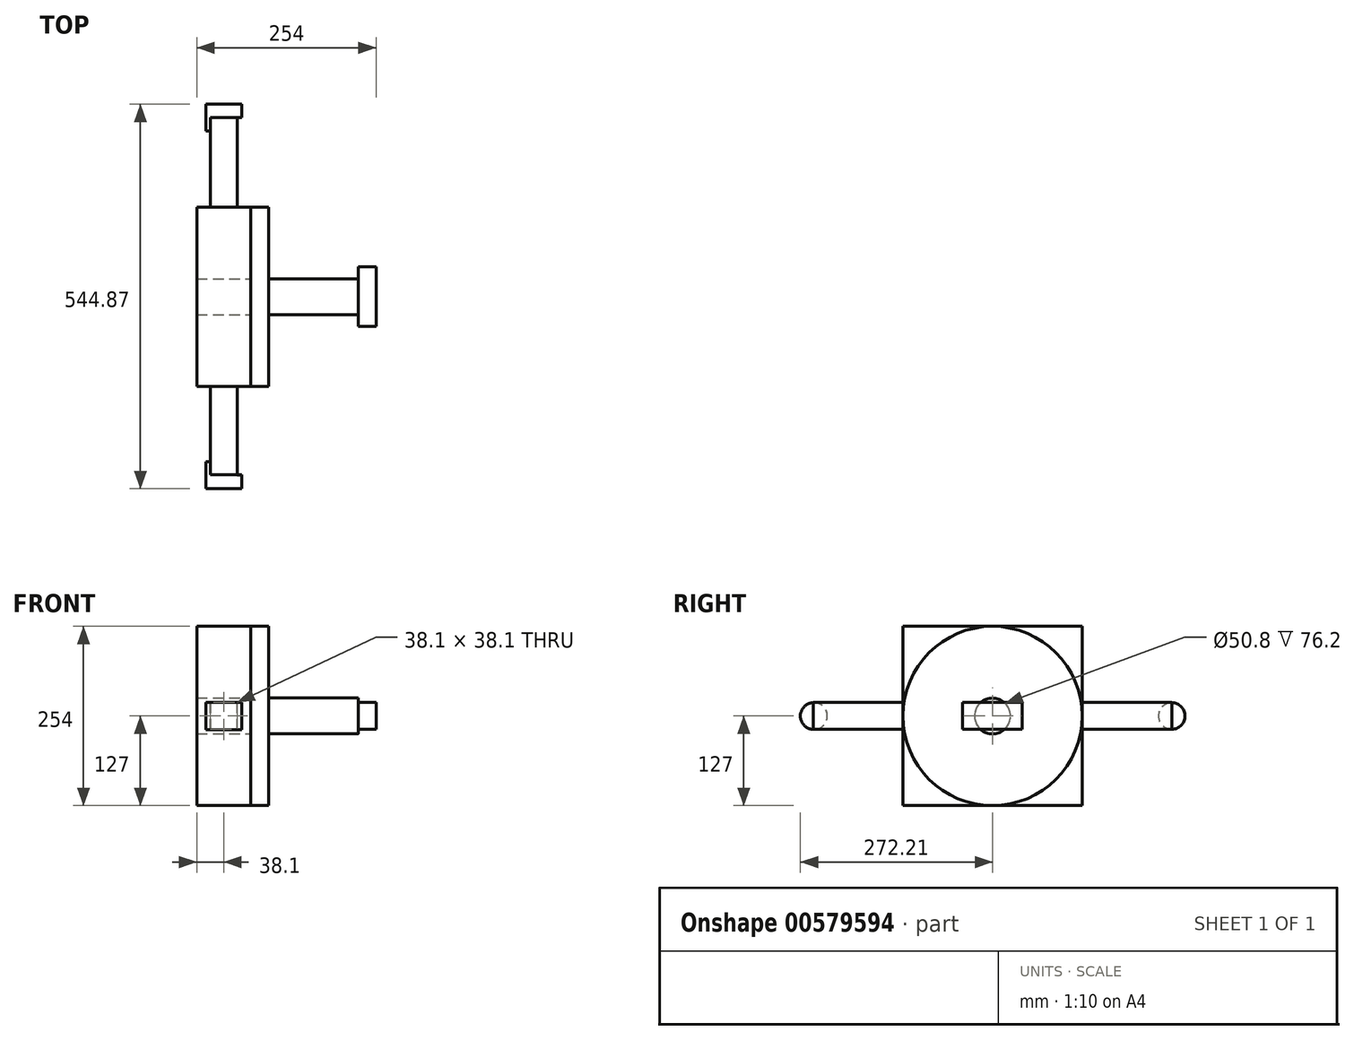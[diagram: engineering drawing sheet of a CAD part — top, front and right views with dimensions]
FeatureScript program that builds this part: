
annotation { "Feature Type Name" : "Feature", "Feature Type Description" : "" }
export const myFeature = defineFeature(function(context is Context, id is Id, definition is map)
    precondition{}
    {
        {
            var Q0;
            Q0=qCreatedBy(makeId("Right.planeOp"),FACE);
            var sketch = newSketch(context, id + "F0", { "sketchPlane" : qUnion([Q0])});
            skCircle(sketch, "E0", {"center": v(0, 0) * mm, "radius": 25.4 * mm});
            skSolve(sketch);
        }
        {
            var Q0;
            Q0=makeQuery(id+"F0.imprint","IMPRINT",FACE,{"disambiguationData":[TD([[makeQuery(id+"F0.imprint","IMPRINT",EDGE,{"derivedFrom":sQuery(id+"F0.wireOp",EDGE,"E0")}),1.0]])]});
            extrude(context, id + "F1", {"entities" : qUnion([Q0]), "depth" : 127 * mm, "offsetDistance" : 25.4 * mm});
        }
        {
            var Q0;
            Q0=makeQuery(id+"F1.opExtrude","CAP_FACE",FACE,{"disambiguationData":[OSD([sQuery(id+"F0.wireOp",EDGE,"E0")])],"isStart":false});
            var sketch = newSketch(context, id + "F2", { "sketchPlane" : qUnion([Q0])});
            skLineSegment(sketch, "E1", {"start": v(0, 0) * mm, "end": v(-25.4, 0) * mm});
            skLineSegment(sketch, "E2", {"start": v(-25.4, 0) * mm, "end": v(25.4, 0) * mm});
            skLineSegment(sketch, "E3.bottom", {"start": v(16.8, -19.05) * mm, "end": v(-16.8, -19.05) * mm});
            skLineSegment(sketch, "E3.top", {"start": v(16.8, 19.05) * mm, "end": v(-16.8, 19.05) * mm});
            skLineSegment(sketch, "E3.left", {"start": v(16.8, -19.05) * mm, "end": v(16.8, 19.05) * mm});
            skLineSegment(sketch, "E3.right", {"start": v(-16.8, -19.05) * mm, "end": v(-16.8, 19.05) * mm});
            skPoint(sketch, "E3.middle", {"position": v(0, 0) * mm});
            skSolve(sketch);
        }
        {
            var Q0;
            Q0 = qSketchRegion(id + "F2", true);
            extrude(context, id + "F3", {"entities" : qUnion([Q0]), "operationType" : NewBodyOperationType.ADD, "depth" : 25.4 * mm, "offsetDistance" : 25.4 * mm});
        }
        {
            var Q0;
            Q0=makeQuery(id+"F3.opExtrude","SWEPT_FACE",FACE,{"disambiguationData":[OSD([sQuery(id+"F2.wireOp",EDGE,"E3.left")])]});
            extrude(context, id + "F4", {"entities" : qUnion([Q0]), "operationType" : NewBodyOperationType.ADD, "depth" : 25.4 * mm, "offsetDistance" : 25.4 * mm});
        }
        {
            var Q0;
            Q0=makeQuery(id+"F3.opExtrude","SWEPT_FACE",FACE,{"disambiguationData":[OSD([sQuery(id+"F2.wireOp",EDGE,"E3.right")])]});
            extrude(context, id + "F5", {"entities" : qUnion([Q0]), "operationType" : NewBodyOperationType.ADD, "depth" : 25.4 * mm, "offsetDistance" : 25.4 * mm});
        }
        {
            var Q0;
            Q0=makeQuery(id+"F1.opExtrude","CAP_FACE",FACE,{"disambiguationData":[OSD([sQuery(id+"F0.wireOp",EDGE,"E0")])],"isStart":true});
            var sketch = newSketch(context, id + "F6", { "sketchPlane" : qUnion([Q0])});
            skCircle(sketch, "E4", {"center": v(0, 0) * mm, "radius": 127 * mm});
            skSolve(sketch);
        }
        {
            var Q0;
            Q0=makeQuery(id+"F6.imprint","IMPRINT",FACE,{"disambiguationData":[TD([[makeQuery(id+"F6.imprint","IMPRINT",EDGE,{"derivedFrom":sQuery(id+"F6.wireOp",EDGE,"E4")}),1.0]])]});
            extrude(context, id + "F7", {"entities" : qUnion([Q0]), "depth" : 25.4 * mm, "offsetDistance" : 25.4 * mm});
        }
        {
            var Q0;
            Q0=makeQuery(id+"F1.opExtrude","CAP_FACE",FACE,{"disambiguationData":[OSD([sQuery(id+"F0.wireOp",EDGE,"E0")])],"isStart":true});
            extrude(context, id + "F8", {"entities" : qUnion([Q0]), "depth" : 25.4 * mm, "offsetDistance" : 25.4 * mm});
        }
        {
            var Q0;
            Q0=makeQuery(id+"F7.opExtrude","CAP_FACE",FACE,{"disambiguationData":[OSD([sQuery(id+"F0.wireOp",EDGE,"E0"),sQuery(id+"F6.wireOp",EDGE,"E4")])],"isStart":false});
            var sketch = newSketch(context, id + "F9", { "sketchPlane" : qUnion([Q0])});
            skLineSegment(sketch, "E5.bottom", {"start": v(127, -127) * mm, "end": v(-127, -127) * mm});
            skLineSegment(sketch, "E5.top", {"start": v(127, 127) * mm, "end": v(-127, 127) * mm});
            skLineSegment(sketch, "E5.left", {"start": v(127, -127) * mm, "end": v(127, 127) * mm});
            skLineSegment(sketch, "E5.right", {"start": v(-127, -127) * mm, "end": v(-127, 127) * mm});
            skPoint(sketch, "E5.middle", {"position": v(0, 0) * mm});
            skSolve(sketch);
        }
        {
            var Q0;
            {var subQ0=sQuery(id+"F9.wireOp",EDGE,"E5.left");var subQ1=sQuery(id+"F9.wireOp",EDGE,"E5.top");var subQ2=makeQuery(id+"F9.imprint","INTERSECT",VERTEX,{"derivedFrom":[subQ1,subQ0]});Q0=makeQuery(id+"F9.imprint","IMPRINT",FACE,{"disambiguationData":[TD([[makeQuery(id+"F9.imprint","IMPRINT",EDGE,{"disambiguationData":[TD([[subQ2,-1.0]])],"derivedFrom":subQ1}),1.0]])]});}
            var Q1;
            {var subQ0=sQuery(id+"F9.wireOp",EDGE,"E5.right");var subQ1=sQuery(id+"F9.wireOp",EDGE,"E5.top");var subQ2=makeQuery(id+"F9.imprint","INTERSECT",VERTEX,{"derivedFrom":[subQ1,subQ0]});Q1=makeQuery(id+"F9.imprint","IMPRINT",FACE,{"disambiguationData":[TD([[makeQuery(id+"F9.imprint","IMPRINT",EDGE,{"disambiguationData":[TD([[subQ2,1.0]])],"derivedFrom":subQ1}),1.0]])]});}
            var Q2;
            {var subQ0=sQuery(id+"F9.wireOp",EDGE,"E5.right");var subQ1=sQuery(id+"F9.wireOp",EDGE,"E5.bottom");var subQ2=makeQuery(id+"F9.imprint","INTERSECT",VERTEX,{"derivedFrom":[subQ1,subQ0]});Q2=makeQuery(id+"F9.imprint","IMPRINT",FACE,{"disambiguationData":[TD([[makeQuery(id+"F9.imprint","IMPRINT",EDGE,{"disambiguationData":[TD([[subQ2,1.0]])],"derivedFrom":subQ1}),-1.0]])]});}
            var Q3;
            {var subQ0=sQuery(id+"F9.wireOp",EDGE,"E5.left");var subQ1=sQuery(id+"F9.wireOp",EDGE,"E5.bottom");var subQ2=makeQuery(id+"F9.imprint","INTERSECT",VERTEX,{"derivedFrom":[subQ1,subQ0]});Q3=makeQuery(id+"F9.imprint","IMPRINT",FACE,{"disambiguationData":[TD([[makeQuery(id+"F9.imprint","IMPRINT",EDGE,{"disambiguationData":[TD([[subQ2,-1.0]])],"derivedFrom":subQ1}),-1.0]])]});}
            var Q4;
            Q4=makeQuery(id+"F9.imprint","IMPRINT",FACE,{"disambiguationData":[TD([[makeQuery(id+"F9.imprint","IMPRINT",EDGE,{"derivedFrom":makeQuery(id+"F7.opExtrude","CAP_EDGE",EDGE,{"disambiguationData":[OSD([sQuery(id+"F0.wireOp",EDGE,"E0")])],"isStart":false})}),1.0]])]});
            extrude(context, id + "F10", {"entities" : qUnion([Q0, Q1, Q2, Q3, Q4]), "operationType" : NewBodyOperationType.ADD, "depth" : 76.2 * mm, "offsetDistance" : 25.4 * mm});
        }
        {
            var Q0;
            Q0=makeQuery(id+"F10.opExtrude","SWEPT_FACE",FACE,{"disambiguationData":[OSD([sQuery(id+"F9.wireOp",EDGE,"E5.right")])]});
            var sketch = newSketch(context, id + "F11", { "sketchPlane" : qUnion([Q0])});
            skLineSegment(sketch, "E6", {"start": v(25.4, 127) * mm, "end": v(94.14, 127) * mm});
            skLineSegment(sketch, "E7", {"start": v(94.14, 127) * mm, "end": v(101.6, 127) * mm});
            skLineSegment(sketch, "E8.bottom", {"start": v(44.45, -19.05) * mm, "end": v(82.55, -19.05) * mm});
            skLineSegment(sketch, "E8.top", {"start": v(44.45, 19.05) * mm, "end": v(82.55, 19.05) * mm});
            skLineSegment(sketch, "E8.left", {"start": v(44.45, -19.05) * mm, "end": v(44.45, 19.05) * mm});
            skLineSegment(sketch, "E8.right", {"start": v(82.55, -19.05) * mm, "end": v(82.55, 19.05) * mm});
            skPoint(sketch, "E8.middle", {"position": v(63.5, 0) * mm});
            skSolve(sketch);
        }
        {
            var Q0;
            Q0=makeQuery(id+"F11.imprint","IMPRINT",FACE,{"disambiguationData":[TD([[makeQuery(id+"F11.imprint","IMPRINT",EDGE,{"derivedFrom":sQuery(id+"F11.wireOp",EDGE,"E8.bottom")}),1.0]])]});
            extrude(context, id + "F12", {"entities" : qUnion([Q0]), "operationType" : NewBodyOperationType.ADD, "depth" : 127 * mm, "offsetDistance" : 25.4 * mm});
        }
        {
            var Q0;
            Q0=makeQuery(id+"F10.opExtrude","SWEPT_FACE",FACE,{"disambiguationData":[OSD([sQuery(id+"F9.wireOp",EDGE,"E5.left")])]});
            var sketch = newSketch(context, id + "F13", { "sketchPlane" : qUnion([Q0])});
            skLineSegment(sketch, "E9", {"start": v(-25.4, -127) * mm, "end": v(-101.6, -127) * mm});
            skLineSegment(sketch, "E10.bottom", {"start": v(-44.45, 19.05) * mm, "end": v(-82.55, 19.05) * mm});
            skLineSegment(sketch, "E10.top", {"start": v(-44.45, -19.05) * mm, "end": v(-82.55, -19.05) * mm});
            skLineSegment(sketch, "E10.left", {"start": v(-44.45, 19.05) * mm, "end": v(-44.45, -19.05) * mm});
            skLineSegment(sketch, "E10.right", {"start": v(-82.55, 19.05) * mm, "end": v(-82.55, -19.05) * mm});
            skPoint(sketch, "E10.middle", {"position": v(-63.5, 0) * mm});
            skSolve(sketch);
        }
        {
            var Q0;
            Q0=makeQuery(id+"F13.imprint","IMPRINT",FACE,{"disambiguationData":[TD([[makeQuery(id+"F13.imprint","IMPRINT",EDGE,{"derivedFrom":sQuery(id+"F13.wireOp",EDGE,"E10.bottom")}),1.0]])]});
            extrude(context, id + "F14", {"entities" : qUnion([Q0]), "operationType" : NewBodyOperationType.ADD, "depth" : 127 * mm, "offsetDistance" : 25.4 * mm});
        }
        {
            var Q0;
            Q0=makeQuery(id+"F12.opExtrude","SWEPT_FACE",FACE,{"disambiguationData":[OSD([sQuery(id+"F11.wireOp",EDGE,"E8.right")])]});
            cPlane(context, id + "F15", {"entities" : qUnion([Q0]), "cplaneType" : CPlaneType.OFFSET, "offset" : 19.05 * mm, "oppositeDirection" : true, "width" : 152.4 * mm, "height" : 152.4 * mm});
        }
        {
            var Q0;
            Q0=qCreatedBy(id+"F15.planeOp",FACE);
            var sketch = newSketch(context, id + "F16", { "sketchPlane" : qUnion([Q0])});
            skCircle(sketch, "E11", {"center": v(-253.82, 0) * mm, "radius": 18.84 * mm});
            skSolve(sketch);
        }
        {
            var Q0;
            Q0=makeQuery(id+"F16.imprint","IMPRINT",FACE,{"disambiguationData":[TD([[makeQuery(id+"F16.imprint","IMPRINT",EDGE,{"derivedFrom":sQuery(id+"F16.wireOp",EDGE,"E11")}),1.0]])]});
            extrude(context, id + "F17", {"entities" : qUnion([Q0]), "operationType" : NewBodyOperationType.ADD, "depth" : 25.4 * mm, "offsetDistance" : 25.4 * mm});
        }
        {
            var Q0;
            Q0=makeQuery(id+"F17.opExtrude","CAP_FACE",FACE,{"disambiguationData":[OSD([sQuery(id+"F16.wireOp",EDGE,"E11")])],"isStart":true});
            extrude(context, id + "F18", {"entities" : qUnion([Q0]), "operationType" : NewBodyOperationType.ADD, "depth" : 25.4 * mm, "offsetDistance" : 25.4 * mm});
        }
        {
            var Q0;
            Q0=qCreatedBy(id+"F15.planeOp",FACE);
            var sketch = newSketch(context, id + "F19", { "sketchPlane" : qUnion([Q0])});
            skCircle(sketch, "E12", {"center": v(253.14, 0) * mm, "radius": 19.08 * mm});
            skSolve(sketch);
        }
        {
            var Q0;
            Q0=makeQuery(id+"F19.imprint","IMPRINT",FACE,{"disambiguationData":[TD([[makeQuery(id+"F19.imprint","IMPRINT",EDGE,{"derivedFrom":sQuery(id+"F19.wireOp",EDGE,"E12")}),1.0]])]});
            extrude(context, id + "F20", {"entities" : qUnion([Q0]), "operationType" : NewBodyOperationType.ADD, "depth" : 25.4 * mm, "offsetDistance" : 25.4 * mm});
        }
        {
            var Q0;
            Q0=makeQuery(id+"F20.opExtrude","CAP_FACE",FACE,{"disambiguationData":[OSD([sQuery(id+"F19.wireOp",EDGE,"E12")])],"isStart":true});
            extrude(context, id + "F21", {"entities" : qUnion([Q0]), "operationType" : NewBodyOperationType.ADD, "depth" : 25.4 * mm, "offsetDistance" : 25.4 * mm});
        }
    });
